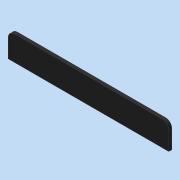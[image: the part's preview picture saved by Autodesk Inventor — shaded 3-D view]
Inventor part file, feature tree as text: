
AUTODESK INVENTOR PART (.ipt)
format: ipt  version: 2020 (Build 240168000, 168)  size: 83,456 bytes
history: native  units: mm
features: other x1, extrude x1, fillet x1
ambient origin geometry x8: Origin, YZ Plane, XZ Plane, XY Plane, X Axis, Y Axis, Z Axis, Center Point
bodies: Body1 (feature_tree)
feature tree (3):
  other  "實體1"
  extrude  "擠出1"  Depth=20.0mm
  fillet  "圓角1"  Radius=130.0mm
